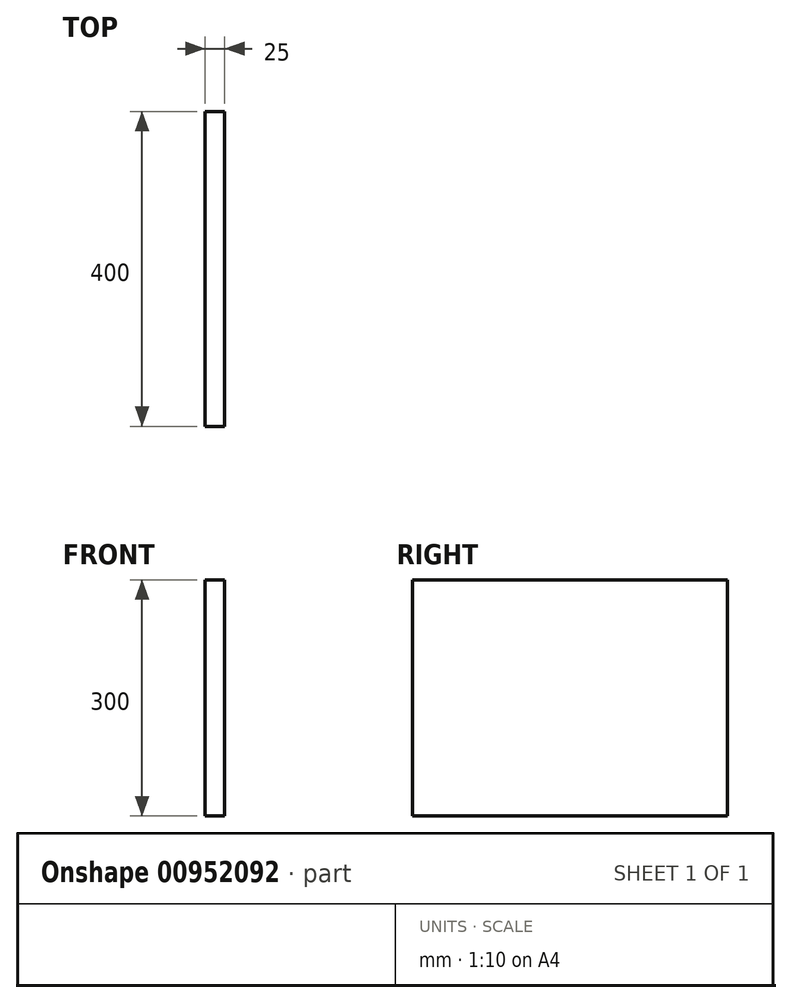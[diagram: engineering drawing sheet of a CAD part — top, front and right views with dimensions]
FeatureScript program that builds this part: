
annotation { "Feature Type Name" : "Feature", "Feature Type Description" : "" }
export const myFeature = defineFeature(function(context is Context, id is Id, definition is map)
    precondition{}
    {
        {
            var Q0;
            Q0=qCreatedBy(makeId("Right.planeOp"),FACE);
            var sketch = newSketch(context, id + "F0", { "sketchPlane" : qUnion([Q0])});
            skLineSegment(sketch, "E0.bottom", {"start": v(-200, 150) * mm, "end": v(200, 150) * mm});
            skLineSegment(sketch, "E0.top", {"start": v(-200, -150) * mm, "end": v(200, -150) * mm});
            skLineSegment(sketch, "E0.left", {"start": v(-200, 150) * mm, "end": v(-200, -150) * mm});
            skLineSegment(sketch, "E0.right", {"start": v(200, 150) * mm, "end": v(200, -150) * mm});
            skPoint(sketch, "E0.middle", {"position": v(0, 0) * mm});
            skSolve(sketch);
        }
        {
            var Q0;
            Q0=makeQuery(id+"F0.imprint","IMPRINT",FACE,{"disambiguationData":[TD([[makeQuery(id+"F0.imprint","IMPRINT",EDGE,{"derivedFrom":sQuery(id+"F0.wireOp",EDGE,"E0.bottom")}),-1.0]])]});
            extrude(context, id + "F1", {"entities" : qUnion([Q0]), "depth" : 25 * mm, "offsetDistance" : 25 * mm});
        }
    });
